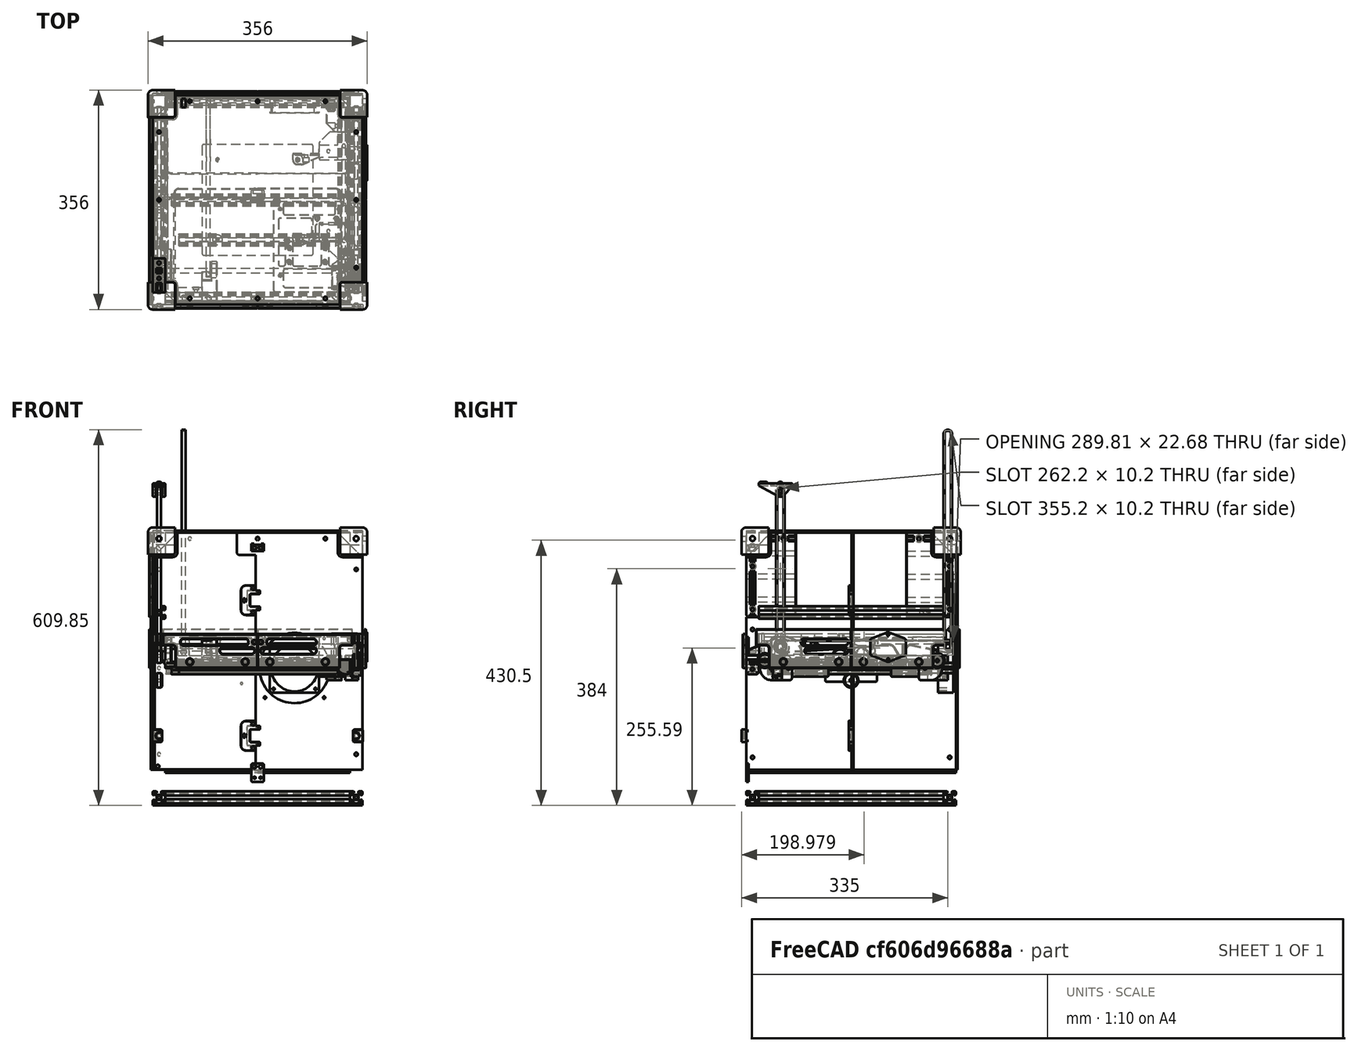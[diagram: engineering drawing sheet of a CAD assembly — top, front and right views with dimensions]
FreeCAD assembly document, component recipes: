
FREECAD ASSEMBLY — COMPONENT RECIPES ("assembly")

This assembly document has 26 components, labeled P0..P25 below (a component is one placed body or linked part). 25 of them carry a construction recipe — the FreeCAD feature program that regenerates the part from scratch, quoted from this document or its linked companion documents; the rest are supplied as boundary geometry only. No exploded tour is included for this assembly.
NOTE — document 3 of 3 of this assembly tour. The two overview renders and the header above are repeated from document 1; the component sections below continue where the previous document stopped.
COMPONENT P24 — recipe-attached ("frame", modeled in this document).
Construction recipe (the document's own serialized feature program — sketch geometry with constraints, then the solid features built on it; lengths are millimeters unless a unit is written):

FEATURE [PartDesign::Mirrored] Mirrored004
  MirrorPlane = -> YZ_Plane006
  Suppressed = false
  TransformMode = 0
FEATURE [PartDesign::Mirrored] Mirrored005
  MirrorPlane = -> XZ_Plane006
  Suppressed = false
  TransformMode = 0
FEATURE [Sketcher::SketchObject] Sketch
  ArcFitTolerance = 0
  AttachmentSupport = -> [XY_Plane005]
  FullyConstrained = true
  MakeInternals = false
  MapMode = 5
  sketch-geometry (22):
    g0: ArcOfCircle CenterX=-9 CenterY=9 CenterZ=0 NormalX=0 NormalY=0 NormalZ=1 AngleXU=0 Radius=1 StartAngle=1.5708 EndAngle=2.35619
    g1: LineSegment StartX=-9 StartY=10 StartZ=0 EndX=-4.90355 EndY=10 EndZ=0
    g2: LineSegment StartX=-4.55 StartY=9.85355 StartZ=0 EndX=-3.12322 EndY=8.42678 EndZ=0
    g3: LineSegment StartX=-3.3 StartY=8 StartZ=0 EndX=-5.75 EndY=8 EndZ=0
    g4: LineSegment StartX=-5.85355 StartY=6.91421 StartZ=0 EndX=-3.08579 EndY=4.14645 EndZ=0
    g5: LineSegment StartX=-2.73223 StartY=4 StartZ=0 EndX=0 EndY=4 EndZ=0
    g6: LineSegment StartX=-6 StartY=7.75 StartZ=0 EndX=-6 EndY=7.26777 EndZ=0
    g7: ArcOfCircle CenterX=-3.3 CenterY=8.25 CenterZ=0 NormalX=0 NormalY=0 NormalZ=1 AngleXU=0 Radius=0.25 StartAngle=4.71239 EndAngle=7.06858
    g8: ArcOfCircle CenterX=-4.90355 CenterY=9.5 CenterZ=0 NormalX=0 NormalY=0 NormalZ=1 AngleXU=0 Radius=0.5 StartAngle=0.785398 EndAngle=1.5708
    g9: GeomPoint [constr] X=-3.05 Y=8.25 Z=0
    g10: ArcOfCircle CenterX=-2.73223 CenterY=4.5 CenterZ=0 NormalX=0 NormalY=0 NormalZ=1 AngleXU=0 Radius=0.5 StartAngle=3.92699 EndAngle=4.71239
    g11: GeomPoint [constr] X=-2.93934 Y=4 Z=0
    g12: ArcOfCircle CenterX=-5.5 CenterY=7.26777 CenterZ=0 NormalX=0 NormalY=0 NormalZ=1 AngleXU=0 Radius=0.5 StartAngle=3.14159 EndAngle=3.92699
    g13: GeomPoint [constr] X=-6 Y=7.06066 Z=0
    g14: ArcOfCircle CenterX=-5.75 CenterY=7.75 CenterZ=0 NormalX=0 NormalY=0 NormalZ=1 AngleXU=0 Radius=0.25 StartAngle=1.5708 EndAngle=3.14159
    g15: GeomPoint [constr] X=-6 Y=8 Z=0
    g16: ArcOfCircle CenterX=0 CenterY=0 CenterZ=0 NormalX=0 NormalY=0 NormalZ=1 AngleXU=0 Radius=2.75 StartAngle=1.5708 EndAngle=2.35619
    g17: GeomPoint [constr] X=0 Y=10 Z=0
    g18: GeomPoint [constr] X=-10 Y=10 Z=0
    g19: LineSegment StartX=-9.70711 StartY=9.70711 StartZ=0 EndX=-1.94454 EndY=1.94454 EndZ=0
    g20: LineSegment StartX=2e-16 StartY=2.75 StartZ=0 EndX=0 EndY=4 EndZ=0
    g21: LineSegment [constr] StartX=-4.46967 StartY=5.53033 StartZ=0 EndX=-5 EndY=5 EndZ=0
  constraints (55):
    c: Radius(g0) = 1
    c: Horizontal(g3)
    c: Parallel(g2,g4)
    c: Vertical(g6)
    c: Tangent(g2,g7) = 1.5708
    c: Tangent(g3,g7) = 1.5708
    c: Tangent(g1,g8) = 1.5708
    c: Tangent(g2,g8) = 1.5708
    c: Radius(g7) = 0.25
    c: Tangent(g1,g0) = 1.5708
    c: PointOnObject(g9,g7)
    c: Horizontal(g9,g7)
    c: PointOnObject(g11,g4)
    c: PointOnObject(g11,g5)
    c: Tangent(g4,g10) = -1.5708
    c: Tangent(g5,g10) = -1.5708
    c: PointOnObject(g13,g4)
    c: PointOnObject(g13,g6)
    c: Tangent(g4,g12) = -1.5708
    c: Tangent(g6,g12) = -1.5708
    c: PointOnObject(g15,g3)
    c: PointOnObject(g15,g6)
    c: Tangent(g3,g14) = -1.5708
    c: Tangent(g6,g14) = -1.5708
    c: Equal(g10,g12)
    c: PointOnObject(g5,g-2)
    c: Coincident(g16,g-1)
    c: PointOnObject(g16,g-2)
    c: PointOnObject(g17,g-2)
    c: PointOnObject(g17,g1)
    c: PointOnObject(g18,g1)
    c: Coincident(g19,g0)
    c: Coincident(g16,g19)
    c: PointOnObject(g0,g19)
    c: PointOnObject(g18,g19)
    c: Parallel(g19,g4)
    c: DistanceX(g18) = -10
    c: DistanceY(g18) = 10
    c: PointOnObject(g16,g19)
    c: Horizontal(g5)
    c: Coincident(g20,g16)
    c: Coincident(g20,g5)
    c: Horizontal(g1)
    c: DistanceX(g15) = -6
    c: DistanceX(g9) = -3.05
    c: DistanceY(g3,g1) = 2
    c: Radius(g10) = 0.5
    c: Radius(g16) = 2.75
    c: DistanceY(g5) = 4
    c: PointOnObject(g21,g4)
    c: Perpendicular(g19,g21)
    c: Distance(g21) = 0.75
    c: Symmetric(g16,g18,g21)
    c: Equal(g14,g7)
    c: Equal(g8,g12)
FEATURE [PartDesign::ShapeBinder] ShapeBinder001
  Support = -> [Sketch]
  TraceSupport = false
FEATURE [PartDesign::Pad] Pad001
  Direction = (0,0,1)
  Length = 440
  Length2 = 10
  Midplane = true
  Profile = -> ShapeBinder001
  Suppressed = false
  Type = 0
  expr: Length = Spreadsheet.height
FEATURE [PartDesign::Mirrored] Mirrored003
  MirrorPlane = -> Pad001 [Face4]
  Suppressed = false
  TransformMode = 0
FEATURE [PartDesign::MultiTransform] MultiTransform001
  BaseFeature = -> Pad001
  Originals = -> [Pad001]
  Refine = true
  Suppressed = false
  TransformMode = 0
  Transformations = -> [Mirrored003,Mirrored004,Mirrored005]
FEATURE [PartDesign::Body] Body001  label="vertical-extrusion"
  AllowCompound = false
  Group = -> [ShapeBinder001,Pad001,MultiTransform001,Mirrored003,Mirrored004,Mirrored005]
  Origin = -> Origin006
  Placement = pos=(160,160,0) rot=(0,0,1;0rad)
  Tip = -> MultiTransform001
  expr: .Placement.Base.x = Spreadsheet.side_length / 2 - 10
  expr: .Placement.Base.y = Spreadsheet.side_length / 2 - 10
FEATURE [PartDesign::Pad] Pad
  Direction = (0,0,1)
  Length = 300
  Length2 = 10
  Midplane = true
  Profile = -> Sketch
  ReferenceAxis = -> Sketch [N_Axis]
  Suppressed = false
  Type = 0
  expr: Length = Spreadsheet.side_length - 40
FEATURE [PartDesign::Mirrored] Mirrored
  MirrorPlane = -> Pad [Face4]
  Suppressed = false
  TransformMode = 0
FEATURE [PartDesign::Mirrored] Mirrored001
  MirrorPlane = -> Sketch [V_Axis]
  Suppressed = false
  TransformMode = 0
FEATURE [PartDesign::Mirrored] Mirrored002
  MirrorPlane = -> XZ_Plane005
  Suppressed = false
  TransformMode = 0
FEATURE [PartDesign::MultiTransform] MultiTransform
  BaseFeature = -> Pad
  Originals = -> [Pad]
  Refine = true
  Suppressed = false
  TransformMode = 0
  Transformations = -> [Mirrored,Mirrored001,Mirrored002]
FEATURE [PartDesign::Body] Body  label="horizontal-extrusion"
  AllowCompound = false
  Group = -> [Sketch,Pad,MultiTransform,Mirrored,Mirrored001,Mirrored002]
  Origin = -> Origin005
  Placement = pos=(0,160,210) rot=(0,1,0;1.5708rad)
  Tip = -> MultiTransform
  expr: .Placement.Base.y = Spreadsheet.side_length / 2 - 10
  expr: .Placement.Base.z = Spreadsheet.height / 2 - 10
FEATURE [Sketcher::SketchObject] Sketch405
  ArcFitTolerance = 1e-06
  AttachmentSupport = -> [XY_Plane267]
  FullyConstrained = true
  MakeInternals = false
  MapMode = 5
  expr: Constraints[18] = Spreadsheet.side_length
  expr: Constraints[9] = Spreadsheet.side_length - 40
  sketch-geometry (8):
    g0: LineSegment [constr] StartX=-150 StartY=170 StartZ=0 EndX=-150 EndY=-170 EndZ=0
    g1: LineSegment [constr] StartX=-150 StartY=-170 StartZ=0 EndX=150 EndY=-170 EndZ=0
    g2: LineSegment [constr] StartX=150 StartY=-170 StartZ=0 EndX=150 EndY=170 EndZ=0
    g3: LineSegment [constr] StartX=150 StartY=170 StartZ=0 EndX=-150 EndY=170 EndZ=0
    g4: LineSegment StartX=-150 StartY=170 StartZ=0 EndX=150 EndY=170 EndZ=0
    g5: LineSegment StartX=150 StartY=170 StartZ=0 EndX=150 EndY=-170 EndZ=0
    g6: LineSegment StartX=150 StartY=-170 StartZ=0 EndX=-150 EndY=-170 EndZ=0
    g7: LineSegment StartX=-150 StartY=-170 StartZ=0 EndX=-150 EndY=170 EndZ=0
  constraints (19):
    c: Coincident(g0,g1)
    c: Coincident(g1,g2)
    c: Coincident(g2,g3)
    c: Coincident(g3,g0)
    c: Vertical(g0)
    c: Vertical(g2)
    c: Horizontal(g1)
    c: Horizontal(g3)
    c: Symmetric(g1,g0,g-1)
    c: DistanceX(g3,g3) = 300
    c: Coincident(g7,g0)
    c: Coincident(g7,g4)
    c: Coincident(g5,g2)
    c: Coincident(g5,g4)
    c: Coincident(g7,g0)
    c: Coincident(g7,g6)
    c: Coincident(g6,g1)
    c: Coincident(g6,g5)
    c: DistanceY(g5,g5) = 340
FEATURE [PartDesign::Pad] Pad088
  Direction = (0,0,1)
  Length = 3
  Length2 = 10
  Profile = -> Sketch405
  ReferenceAxis = -> Sketch405 [N_Axis]
  Suppressed = false
  Type = 0
FEATURE [Sketcher::SketchObject] Sketch406
  ArcFitTolerance = 1e-06
  AttachmentSupport = -> [XY_Plane267]
  FullyConstrained = true
  MakeInternals = false
  MapMode = 5
  expr: Constraints[0] = Spreadsheet.side_length / 2
  sketch-geometry (7):
    g0: GeomPoint X=170 Y=170 Z=0
    g1: LineSegment [constr] StartX=170 StartY=0 StartZ=0 EndX=170 EndY=170 EndZ=0
    g2: LineSegment [constr] StartX=170 StartY=170 StartZ=0 EndX=0 EndY=170 EndZ=0
    g3: LineSegment StartX=170 StartY=170 StartZ=0 EndX=150 EndY=170 EndZ=0
    g4: LineSegment StartX=150 StartY=170 StartZ=0 EndX=150 EndY=150 EndZ=0
    g5: LineSegment StartX=150 StartY=150 StartZ=0 EndX=170 EndY=150 EndZ=0
    g6: LineSegment StartX=170 StartY=150 StartZ=0 EndX=170 EndY=170 EndZ=0
  constraints (19):
    c: DistanceX(g0) = 170
    c: PointOnObject(g1,g-1)
    c: Coincident(g1,g0)
    c: Vertical(g1)
    c: Coincident(g1,g2)
    c: PointOnObject(g2,g-2)
    c: Horizontal(g2)
    c: Equal(g2,g1)
    c: Coincident(g3,g0)
    c: PointOnObject(g3,g2)
    c: Coincident(g3,g4)
    c: Vertical(g4)
    c: PointOnObject(g5,g1)
    c: Horizontal(g5)
    c: Coincident(g5,g6)
    c: Coincident(g6,g3)
    c: Equal(g5,g4)
    c: DistanceY(g4,g4) = 20
    c: Coincident(g5,g4)
FEATURE [PartDesign::Pocket] Pocket281
  BaseFeature = -> Pad088
  Direction = (0,0,-1)
  Length = 5
  Length2 = 5
  Midplane = true
  Profile = -> Sketch406
  ReferenceAxis = -> Sketch406 [N_Axis]
  Suppressed = false
  Type = 1
FEATURE [PartDesign::PolarPattern] PolarPattern004
  Angle = 360
  Axis = -> Z_Axis267
  BaseFeature = -> Pocket281
  Mode = 0
  Occurrences = 4
  Offset = 120
  Originals = -> [Pocket281]
  Suppressed = false
  TransformMode = 0
FEATURE [Sketcher::SketchObject] Sketch407
  ArcFitTolerance = 1e-06
  AttachmentSupport = -> [XY_Plane267]
  FullyConstrained = true
  MakeInternals = false
  MapMode = 5
  expr: Constraints[22] = Spreadsheet.side_length / 2
  sketch-geometry (14):
    g0: LineSegment StartX=115 StartY=170 StartZ=0 EndX=115 EndY=149 EndZ=0
    g1: LineSegment StartX=115 StartY=149 StartZ=0 EndX=125 EndY=149 EndZ=0
    g2: LineSegment StartX=125 StartY=149 StartZ=0 EndX=125 EndY=170 EndZ=0
    g3: LineSegment StartX=125 StartY=170 StartZ=0 EndX=115 EndY=170 EndZ=0
    g4: LineSegment StartX=154 StartY=-105 StartZ=0 EndX=154 EndY=-125 EndZ=0
    g5: LineSegment StartX=154 StartY=-125 StartZ=0 EndX=170 EndY=-125 EndZ=0
    g6: LineSegment StartX=170 StartY=-125 StartZ=0 EndX=170 EndY=-105 EndZ=0
    g7: LineSegment StartX=170 StartY=-105 StartZ=0 EndX=154 EndY=-105 EndZ=0
    g8: GeomPoint X=170 Y=-170 Z=0
    g9: GeomPoint X=170 Y=170 Z=0
    g10: LineSegment [constr] StartX=0 StartY=-170 StartZ=0 EndX=170 EndY=-170 EndZ=0
    g11: LineSegment [constr] StartX=170 StartY=-170 StartZ=0 EndX=170 EndY=0 EndZ=0
    g12: GeomPoint [constr] X=120 Y=170 Z=0
    g13: GeomPoint [constr] X=170 Y=-115 Z=0
  constraints (35):
    c: Coincident(g0,g1)
    c: Coincident(g1,g2)
    c: Coincident(g2,g3)
    c: Coincident(g3,g0)
    c: Vertical(g0)
    c: Vertical(g2)
    c: Horizontal(g1)
    c: Horizontal(g3)
    c: Coincident(g4,g5)
    c: Coincident(g5,g6)
    c: Coincident(g6,g7)
    c: Coincident(g7,g4)
    c: Vertical(g4)
    c: Vertical(g6)
    c: Horizontal(g5)
    c: Horizontal(g7)
    c: PointOnObject(g10,g-2)
    c: Coincident(g10,g8)
    c: Coincident(g10,g11)
    c: PointOnObject(g11,g-1)
    c: Vertical(g11)
    c: Horizontal(g10)
    c: DistanceX(g8) = 170
    c: Equal(g11,g10)
    c: Symmetric(g9,g8,g-1)
    c: PointOnObject(g5,g11)
    c: DistanceX(g5,g5) = 16
    c: DistanceX(g3,g3) = 10
    c: Horizontal(g2,g9)
    c: Symmetric(g3,g3,g12)
    c: DistanceX(g12,g9) = 50
    c: DistanceY(g2,g2) = 21
    c: Symmetric(g6,g6,g13)
    c: DistanceY(g8,g13) = 55
    c: DistanceY(g4,g4) = 20
FEATURE [PartDesign::Pocket] Pocket282
  BaseFeature = -> PolarPattern004
  Direction = (0,0,-1)
  Length = 5
  Length2 = 5
  Midplane = true
  Profile = -> Sketch407
  ReferenceAxis = -> Sketch407 [N_Axis]
  Suppressed = false
  Type = 1
FEATURE [PartDesign::Mirrored] Mirrored009
  BaseFeature = -> Pocket282
  MirrorPlane = -> YZ_Plane267
  Originals = -> [Pocket282]
  Suppressed = false
  TransformMode = 0
FEATURE [Sketcher::SketchObject] Sketch426
  ArcFitTolerance = 1e-06
  AttachmentSupport = -> [XZ_Plane280]
  FullyConstrained = true
  MakeInternals = false
  MapMode = 5
  Placement = pos=(0,0,0) rot=(1,0,0;1.5708rad)
  expr: Constraints[10] = Spreadsheet.height
  expr: Constraints[7] = Spreadsheet.side_length
  sketch-geometry (5):
    g0: LineSegment StartX=-170 StartY=220 StartZ=0 EndX=-170 EndY=-165 EndZ=0
    g1: LineSegment StartX=-170 StartY=-165 StartZ=0 EndX=170 EndY=-165 EndZ=0
    g2: LineSegment StartX=170 StartY=-165 StartZ=0 EndX=170 EndY=220 EndZ=0
    g3: LineSegment StartX=170 StartY=220 StartZ=0 EndX=-170 EndY=220 EndZ=0
    g4: GeomPoint X=170 Y=-220 Z=0
  constraints (12):
    c: Coincident(g0,g1)
    c: Coincident(g1,g2)
    c: Coincident(g2,g3)
    c: Coincident(g3,g0)
    c: Vertical(g0)
    c: Vertical(g2)
    c: Horizontal(g1)
    c: DistanceX(g3,g3) = 340
    c: Symmetric(g2,g0,g-2)
    c: Symmetric(g4,g2,g-1)
    c: DistanceY(g4,g2) = 440
    c: DistanceY(g4,g1) = 55
FEATURE [PartDesign::Pad] Pad091
  Direction = (0,-1,2e-16)
  Length = 3
  Length2 = 10
  Placement = pos=(0,0,0) rot=(1,0,0;1.5708rad)
  Profile = -> Sketch426
  ReferenceAxis = -> Sketch426 [N_Axis]
  Reversed = true
  Suppressed = false
  Type = 0
FEATURE [Sketcher::SketchObject] Sketch427
  ArcFitTolerance = 1e-06
  AttachmentSupport = -> [XZ_Plane280]
  FullyConstrained = true
  MakeInternals = false
  MapMode = 5
  Placement = pos=(0,0,0) rot=(1,0,0;1.5708rad)
  expr: Constraints[0] = Spreadsheet.height / 2
  expr: Constraints[1] = Spreadsheet.side_length / 2
  sketch-geometry (11):
    g0: GeomPoint X=170 Y=220 Z=0
    g1: LineSegment StartX=133.5 StartY=187.5 StartZ=0 EndX=133.5 EndY=220 EndZ=0
    g2: LineSegment StartX=133.5 StartY=220 StartZ=0 EndX=170 EndY=220 EndZ=0
    g3: LineSegment StartX=170 StartY=220 StartZ=0 EndX=170 EndY=183.5 EndZ=0
    g4: LineSegment StartX=170 StartY=183.5 StartZ=0 EndX=137.5 EndY=183.5 EndZ=0
    g5: ArcOfCircle CenterX=137.5 CenterY=187.5 CenterZ=0 NormalX=0 NormalY=0 NormalZ=1 AngleXU=0 Radius=4 StartAngle=3.14159 EndAngle=4.71239
    g6: Circle CenterX=0 CenterY=210 CenterZ=0 NormalX=0 NormalY=0 NormalZ=1 AngleXU=0 Radius=2.75
    g7: Circle CenterX=110 CenterY=210 CenterZ=0 NormalX=0 NormalY=0 NormalZ=1 AngleXU=0 Radius=2.75
    g8: Circle CenterX=160 CenterY=160 CenterZ=0 NormalX=0 NormalY=0 NormalZ=1 AngleXU=0 Radius=2.75
    g9: Circle CenterX=160 CenterY=0 CenterZ=0 NormalX=0 NormalY=0 NormalZ=1 AngleXU=0 Radius=2.75
    g10: Circle CenterX=160 CenterY=-140 CenterZ=0 NormalX=0 NormalY=0 NormalZ=1 AngleXU=0 Radius=2.75
  constraints (30):
    c: DistanceY(g0) = 220
    c: DistanceX(g0) = 170
    c: Vertical(g1)
    c: Coincident(g1,g2)
    c: Coincident(g2,g0)
    c: Horizontal(g2)
    c: Coincident(g2,g3)
    c: Vertical(g3)
    c: Coincident(g3,g4)
    c: Tangent(g5,g1) = 1.5708
    c: Tangent(g5,g4) = 1.5708
    c: Horizontal(g4)
    c: DistanceY(g3,g3) = 36.5
    c: Equal(g2,g3)
    c: Radius(g5) = 4
    c: PointOnObject(g6,g-2)
    c: PointOnObject(g9,g-1)
    c: Equal(g7,g8)
    c: Equal(g8,g9)
    c: Equal(g9,g6)
    c: Diameter(g6) = 5.5
    c: Horizontal(g6,g7)
    c: DistanceY(g7,g0) = 10
    c: DistanceX(g7,g0) = 60
    c: DistanceX(g8,g0) = 10
    c: DistanceY(g8,g0) = 60
    c: DistanceY(g10) = -140
    c: Vertical(g10,g9)
    c: Equal(g9,g10)
    c: Vertical(g9,g8)
FEATURE [PartDesign::Pocket] Pocket299
  BaseFeature = -> Pad091
  Direction = (0,1,-2e-16)
  Length = 5
  Length2 = 5
  Placement = pos=(0,0,0) rot=(1,0,0;1.5708rad)
  Profile = -> Sketch427
  ReferenceAxis = -> Sketch427 [N_Axis]
  Suppressed = false
  Type = 1
FEATURE [PartDesign::Mirrored] Mirrored010
  BaseFeature = -> Pocket299
  MirrorPlane = -> YZ_Plane280
  Originals = -> [Pocket299]
  Placement = pos=(0,0,0) rot=(1,0,0;1.5708rad)
  Suppressed = false
  TransformMode = 0
FEATURE [Sketcher::SketchObject] Sketch428
  ArcFitTolerance = 1e-06
  AttachmentSupport = -> [YZ_Plane281]
  FullyConstrained = true
  MakeInternals = false
  MapMode = 5
  Placement = pos=(0,0,0) rot=(0.57735,0.57735,0.57735;2.0944rad)
  expr: Constraints[10] = Spreadsheet.height
  expr: Constraints[28] = Spreadsheet.xy_gantry_height
  expr: Constraints[9] = Spreadsheet.side_length
  sketch-geometry (33):
    g0: GeomPoint X=170 Y=-220 Z=0
    g1: LineSegment [constr] StartX=-170 StartY=220 StartZ=0 EndX=-170 EndY=-165 EndZ=0
    g2: LineSegment StartX=-170 StartY=-165 StartZ=0 EndX=170 EndY=-165 EndZ=0
    g3: LineSegment [constr] StartX=170 StartY=-165 StartZ=0 EndX=170 EndY=220 EndZ=0
    g4: LineSegment [constr] StartX=170 StartY=220 StartZ=0 EndX=-170 EndY=220 EndZ=0
    g5: LineSegment StartX=-170 StartY=-165 StartZ=0 EndX=-170 EndY=82.5 EndZ=0
    g6: LineSegment StartX=-170 StartY=82.5 StartZ=0 EndX=-93.7 EndY=82.5 EndZ=0
    g7: LineSegment StartX=-89.7 StartY=86.5 StartZ=0 EndX=-89.7 EndY=220 EndZ=0
    g8: LineSegment StartX=-89.7 StartY=220 StartZ=0 EndX=89.7 EndY=220 EndZ=0
    g9: LineSegment StartX=89.7 StartY=220 StartZ=0 EndX=89.7 EndY=86.5 EndZ=0
    g10: LineSegment StartX=93.7 StartY=82.5 StartZ=0 EndX=170 EndY=82.5 EndZ=0
    g11: LineSegment StartX=170 StartY=82.5 StartZ=0 EndX=170 EndY=-165 EndZ=0
    g12: GeomPoint X=170 Y=90 Z=0
    g13: ArcOfCircle CenterX=-93.7 CenterY=86.5 CenterZ=0 NormalX=0 NormalY=0 NormalZ=1 AngleXU=0 Radius=4 StartAngle=4.71239 EndAngle=6.28319
    g14: GeomPoint [constr] X=-89.7 Y=82.5 Z=0
    g15: ArcOfCircle CenterX=93.7 CenterY=86.5 CenterZ=0 NormalX=0 NormalY=0 NormalZ=1 AngleXU=0 Radius=4 StartAngle=3.14159 EndAngle=4.71239
    g16: GeomPoint [constr] X=89.7 Y=82.5 Z=0
    g17: Circle CenterX=-160 CenterY=62.5 CenterZ=0 NormalX=0 NormalY=0 NormalZ=1 AngleXU=0 Radius=2.75
    g18: Circle CenterX=-160 CenterY=-145 CenterZ=0 NormalX=0 NormalY=0 NormalZ=1 AngleXU=0 Radius=2.75
    g19: Circle CenterX=160 CenterY=-145 CenterZ=0 NormalX=0 NormalY=0 NormalZ=1 AngleXU=0 Radius=2.75
    g20: Circle CenterX=160 CenterY=62.5 CenterZ=0 NormalX=0 NormalY=0 NormalZ=1 AngleXU=0 Radius=2.75
    g21: LineSegment StartX=-42.1 StartY=20.1 StartZ=0 EndX=-42.1 EndY=-20.1 EndZ=0
    g22: LineSegment StartX=-40.1 StartY=-22.1 StartZ=0 EndX=40.1 EndY=-22.1 EndZ=0
    g23: LineSegment StartX=42.1 StartY=-20.1 StartZ=0 EndX=42.1 EndY=20.1 EndZ=0
    g24: LineSegment StartX=40.1 StartY=22.1 StartZ=0 EndX=-40.1 EndY=22.1 EndZ=0
    g25: ArcOfCircle CenterX=40.1 CenterY=20.1 CenterZ=0 NormalX=0 NormalY=0 NormalZ=1 AngleXU=0 Radius=2 StartAngle=5e-16 EndAngle=1.5708
    g26: GeomPoint [constr] X=42.1 Y=22.1 Z=0
    g27: ArcOfCircle CenterX=40.1 CenterY=-20.1 CenterZ=0 NormalX=0 NormalY=0 NormalZ=1 AngleXU=0 Radius=2 StartAngle=4.71239 EndAngle=6.28319
    g28: GeomPoint [constr] X=42.1 Y=-22.1 Z=0
    g29: ArcOfCircle CenterX=-40.1 CenterY=-20.1 CenterZ=0 NormalX=0 NormalY=0 NormalZ=1 AngleXU=0 Radius=2 StartAngle=3.14159 EndAngle=4.71239
    g30: GeomPoint [constr] X=-42.1 Y=-22.1 Z=0
    g31: ArcOfCircle CenterX=-40.1 CenterY=20.1 CenterZ=0 NormalX=0 NormalY=0 NormalZ=1 AngleXU=0 Radius=2 StartAngle=1.5708 EndAngle=3.14159
    g32: GeomPoint [constr] X=-42.1 Y=22.1 Z=0
  constraints (78):
    c: Coincident(g1,g2)
    c: Coincident(g2,g3)
    c: Coincident(g3,g4)
    c: Coincident(g4,g1)
    c: Vertical(g1)
    c: Vertical(g3)
    c: Horizontal(g2)
    c: Symmetric(g3,g0,g-1)
    c: Symmetric(g3,g1,g-2)
    c: DistanceX(g4,g4) = 340
    c: DistanceY(g0,g3) = 440
    c: DistanceY(g0,g2) = 55
    c: Coincident(g1,g5)
    c: PointOnObject(g5,g1)
    c: Coincident(g5,g6)
    c: Horizontal(g6)
    c: PointOnObject(g7,g4)
    c: Vertical(g7)
    c: Coincident(g7,g8)
    c: PointOnObject(g8,g4)
    c: Coincident(g8,g9)
    c: Vertical(g9)
    c: PointOnObject(g10,g3)
    c: Horizontal(g10)
    c: Coincident(g10,g11)
    c: Coincident(g11,g2)
    c: Symmetric(g16,g14,g-2)
    c: PointOnObject(g12,g3)
    c: DistanceY(g0,g12) = 310
    c: DistanceY(g10,g12) = 7.5
    c: DistanceX(g16,g10) = 80.3
    c: PointOnObject(g14,g6)
    c: PointOnObject(g14,g7)
    c: Tangent(g6,g13) = -1.5708
    c: Tangent(g7,g13) = -1.5708
    c: PointOnObject(g16,g9)
    c: PointOnObject(g16,g10)
    c: Tangent(g9,g15) = -1.5708
    c: Tangent(g10,g15) = -1.5708
    c: Equal(g15,g13)
    c: Radius(g13) = 4
    c: Symmetric(g20,g17,g-2)
    c: Symmetric(g19,g18,g-2)
    c: Equal(g18,g19)
    c: Equal(g19,g20)
    c: Equal(g20,g17)
    c: Diameter(g17) = 5.5
    c: DistanceY(g17,g5) = 20
    c: DistanceX(g5,g17) = 10
    c: DistanceY(g1,g18) = 20
    c: Vertical(g18,g17)
    c: Vertical(g21)
    c: Vertical(g23)
    c: Horizontal(g22)
    c: Horizontal(g24)
    c: Symmetric(g32,g28,g-1)
    c: DistanceY(g28,g26) = 44.2
    c: DistanceX(g32,g26) = 84.2
    c: PointOnObject(g26,g23)
    c: PointOnObject(g26,g24)
    c: Tangent(g23,g25) = -1.5708
    c: Tangent(g24,g25) = -1.5708
    c: PointOnObject(g28,g22)
    c: PointOnObject(g28,g23)
    c: Tangent(g22,g27) = -1.5708
    c: Tangent(g23,g27) = -1.5708
    c: PointOnObject(g30,g21)
    c: PointOnObject(g30,g22)
    c: Tangent(g21,g29) = -1.5708
    c: Tangent(g22,g29) = -1.5708
    c: PointOnObject(g32,g21)
    c: PointOnObject(g32,g24)
    c: Tangent(g21,g31) = -1.5708
    c: Tangent(g24,g31) = -1.5708
    c: Equal(g25,g31)
    c: Equal(g31,g29)
    c: Equal(g29,g27)
    c: Radius(g27) = 2
FEATURE [PartDesign::Pad] Pad092
  Direction = (1,0,0)
  Length = 3
  Length2 = 10
  Placement = pos=(0,0,0) rot=(1,1,1;2.0944rad)
  Profile = -> Sketch428
  ReferenceAxis = -> Sketch428 [N_Axis]
  Suppressed = false
  Type = 0
FEATURE [PartDesign::Body] Body144  label="panel-right"
  AllowCompound = false
  Group = -> [Sketch428,Pad092]
  Origin = -> Origin282
  Placement = pos=(170,0,0) rot=(0,0,1;0rad)
  Tip = -> Pad092
  expr: .Placement.Base.x = Spreadsheet.side_length / 2
FEATURE [Sketcher::SketchObject] Sketch429
  ArcFitTolerance = 1e-06
  AttachmentSupport = -> [XY_Plane282]
  FullyConstrained = true
  MakeInternals = false
  MapMode = 5
  expr: Constraints[10] = Spreadsheet.side_length
  sketch-geometry (4):
    g0: LineSegment StartX=-170 StartY=170 StartZ=0 EndX=-170 EndY=-170 EndZ=0
    g1: LineSegment StartX=-170 StartY=-170 StartZ=0 EndX=170 EndY=-170 EndZ=0
    g2: LineSegment StartX=170 StartY=-170 StartZ=0 EndX=170 EndY=170 EndZ=0
    g3: LineSegment StartX=170 StartY=170 StartZ=0 EndX=-170 EndY=170 EndZ=0
  constraints (11):
    c: Coincident(g0,g1)
    c: Coincident(g1,g2)
    c: Coincident(g2,g3)
    c: Coincident(g3,g0)
    c: Vertical(g0)
    c: Vertical(g2)
    c: Horizontal(g1)
    c: Horizontal(g3)
    c: Symmetric(g1,g0,g-1)
    c: Equal(g2,g3)
    c: DistanceX(g3,g3) = 340
FEATURE [PartDesign::Pad] Pad093
  Direction = (0,0,1)
  Length = 3
  Length2 = 10
  Profile = -> Sketch429
  ReferenceAxis = -> Sketch429 [N_Axis]
  Suppressed = false
  Type = 0
FEATURE [Sketcher::SketchObject] Sketch430
  ArcFitTolerance = 1e-06
  AttachmentSupport = -> [XY_Plane282]
  FullyConstrained = true
  MakeInternals = false
  MapMode = 5
  expr: Constraints[0] = Spreadsheet.side_length / 2
  sketch-geometry (12):
    g0: GeomPoint X=170 Y=170 Z=0
    g1: LineSegment [constr] StartX=170 StartY=0 StartZ=0 EndX=170 EndY=170 EndZ=0
    g2: LineSegment [constr] StartX=170 StartY=170 StartZ=0 EndX=0 EndY=170 EndZ=0
    g3: LineSegment StartX=170 StartY=170 StartZ=0 EndX=133.5 EndY=170 EndZ=0
    g4: LineSegment StartX=133.5 StartY=170 StartZ=0 EndX=133.5 EndY=137.5 EndZ=0
    g5: LineSegment StartX=137.5 StartY=133.5 StartZ=0 EndX=170 EndY=133.5 EndZ=0
    g6: LineSegment StartX=170 StartY=133.5 StartZ=0 EndX=170 EndY=170 EndZ=0
    g7: ArcOfCircle CenterX=137.5 CenterY=137.5 CenterZ=0 NormalX=0 NormalY=0 NormalZ=1 AngleXU=0 Radius=4 StartAngle=3.14159 EndAngle=4.71239
    g8: GeomPoint [constr] X=133.5 Y=133.5 Z=0
    g9: Circle CenterX=110 CenterY=160 CenterZ=0 NormalX=0 NormalY=0 NormalZ=1 AngleXU=0 Radius=2.75
    g10: Circle CenterX=160 CenterY=110 CenterZ=0 NormalX=0 NormalY=0 NormalZ=1 AngleXU=0 Radius=2.75
    g11: Circle CenterX=0 CenterY=160 CenterZ=0 NormalX=0 NormalY=0 NormalZ=1 AngleXU=0 Radius=2.75
  constraints (32):
    c: DistanceX(g0) = 170
    c: PointOnObject(g1,g-1)
    c: Coincident(g1,g0)
    c: Coincident(g1,g2)
    c: PointOnObject(g2,g-2)
    c: Horizontal(g2)
    c: Vertical(g1)
    c: Equal(g2,g1)
    c: Coincident(g3,g4)
    c: Coincident(g5,g6)
    c: Coincident(g6,g3)
    c: Horizontal(g3)
    c: Horizontal(g5)
    c: Vertical(g4)
    c: Vertical(g6)
    c: Coincident(g3,g0)
    c: Equal(g6,g3)
    c: DistanceX(g3,g3) = 36.5
    c: PointOnObject(g8,g4)
    c: PointOnObject(g8,g5)
    c: Tangent(g4,g7) = -1.5708
    c: Tangent(g5,g7) = -1.5708
    c: Radius(g7) = 4
    c: PointOnObject(g11,g-2)
    c: Equal(g11,g9)
    c: Equal(g9,g10)
    c: Horizontal(g9,g11)
    c: DistanceX(g10,g0) = 10
    c: DistanceY(g9,g0) = 10
    c: Diameter(g9) = 5.5
    c: DistanceY(g10,g0) = 60
    c: DistanceX(g9,g0) = 60
FEATURE [PartDesign::Pocket] Pocket300
  BaseFeature = -> Pad093
  Direction = (0,0,-1)
  Length = 5
  Length2 = 5
  Midplane = true
  Profile = -> Sketch430
  ReferenceAxis = -> Sketch430 [N_Axis]
  Suppressed = false
  Type = 1
FEATURE [PartDesign::PolarPattern] PolarPattern005
  Angle = 360
  Axis = -> Z_Axis282
  BaseFeature = -> Pocket300
  Mode = 0
  Occurrences = 4
  Offset = 120
  Originals = -> [Pocket300]
  Suppressed = false
  TransformMode = 0
FEATURE [PartDesign::Body] Body145  label="panel-top"
  AllowCompound = false
  Group = -> [Sketch429,Pad093,Sketch430,Pocket300,PolarPattern005]
  Origin = -> Origin283
  Placement = pos=(0,0,220) rot=(0,0,1;0rad)
  Tip = -> PolarPattern005
  expr: .Placement.Base.z = Spreadsheet.height / 2
FEATURE [PartDesign::FeatureBase] Clone009
  BaseFeature = -> Body146
  Suppressed = false
FEATURE [PartDesign::Body] Body148
  AllowCompound = false
  Group = -> [Clone009]
  Origin = -> Origin286
  Placement = pos=(-160,-170,110) rot=(0,0,1;0rad)
  Tip = -> Clone009
  expr: .Placement.Base.x = -Spreadsheet.side_length / 2 + 10
  expr: .Placement.Base.y = -Spreadsheet.side_length / 2
FEATURE [Sketcher::SketchObject] Sketch450
  ArcFitTolerance = 1e-06
  AttachmentSupport = -> [XZ_Plane289]
  FullyConstrained = true
  MakeInternals = false
  MapMode = 5
  Placement = pos=(0,0,0) rot=(1,0,0;1.5708rad)
  sketch-geometry (12):
    g0: LineSegment StartX=-10 StartY=8 StartZ=0 EndX=-10 EndY=-18 EndZ=0
    g1: LineSegment StartX=-8 StartY=-20 StartZ=0 EndX=8 EndY=-20 EndZ=0
    g2: LineSegment StartX=10 StartY=-18 StartZ=0 EndX=10 EndY=8 EndZ=0
    g3: LineSegment StartX=8 StartY=10 StartZ=0 EndX=-8 EndY=10 EndZ=0
    g4: ArcOfCircle CenterX=-8 CenterY=8 CenterZ=0 NormalX=0 NormalY=0 NormalZ=1 AngleXU=0 Radius=2 StartAngle=1.5708 EndAngle=3.14159
    g5: GeomPoint [constr] X=-10 Y=10 Z=0
    g6: ArcOfCircle CenterX=8 CenterY=8 CenterZ=0 NormalX=0 NormalY=0 NormalZ=1 AngleXU=0 Radius=2 StartAngle=1e-16 EndAngle=1.5708
    g7: GeomPoint [constr] X=10 Y=10 Z=0
    g8: ArcOfCircle CenterX=8 CenterY=-18 CenterZ=0 NormalX=0 NormalY=0 NormalZ=1 AngleXU=0 Radius=2 StartAngle=4.71239 EndAngle=6.28319
    g9: GeomPoint [constr] X=10 Y=-20 Z=0
    g10: ArcOfCircle CenterX=-8 CenterY=-18 CenterZ=0 NormalX=0 NormalY=0 NormalZ=1 AngleXU=0 Radius=2 StartAngle=3.14159 EndAngle=4.71239
    g11: GeomPoint [constr] X=-10 Y=-20 Z=0
  constraints (27):
    c: Vertical(g0)
    c: Vertical(g2)
    c: Horizontal(g1)
    c: DistanceY(g7) = 10
    c: Symmetric(g7,g5,g-2)
    c: DistanceX(g5,g7) = 20
    c: DistanceY(g9) = -20
    c: PointOnObject(g5,g0)
    c: PointOnObject(g5,g3)
    c: Tangent(g0,g4) = -1.5708
    c: Tangent(g3,g4) = -1.5708
    c: PointOnObject(g7,g2)
    c: PointOnObject(g7,g3)
    c: Tangent(g2,g6) = -1.5708
    c: Tangent(g3,g6) = -1.5708
    c: PointOnObject(g9,g1)
    c: PointOnObject(g9,g2)
    c: Tangent(g1,g8) = -1.5708
    c: Tangent(g2,g8) = -1.5708
    c: PointOnObject(g11,g0)
    c: PointOnObject(g11,g1)
    c: Tangent(g0,g10) = -1.5708
    c: Tangent(g1,g10) = -1.5708
    c: Equal(g10,g8)
    c: Equal(g10,g6)
    c: Equal(g10,g4)
    c: Radius(g10) = 2
FEATURE [PartDesign::Pad] Pad099
  Direction = (0,-1,2e-16)
  Length = 4
  Length2 = 10
  Placement = pos=(0,0,0) rot=(1,0,0;1.5708rad)
  Profile = -> Sketch450
  ReferenceAxis = -> Sketch450 [N_Axis]
  Reversed = true
  Suppressed = false
  Type = 0
FEATURE [Sketcher::SketchObject] Sketch451
  ArcFitTolerance = 1e-06
  AttachmentOffset = pos=(0,0,-1) rot=(0,0,1;0rad)
  AttachmentSupport = -> [XZ_Plane289]
  FullyConstrained = true
  MakeInternals = false
  MapMode = 5
  Placement = pos=(0,1,-2e-16) rot=(1,0,0;1.5708rad)
  sketch-geometry (14):
    g0: LineSegment StartX=-2.25 StartY=-14.5877 StartZ=0 EndX=-2.25 EndY=-11.4123 EndZ=0
    g1: LineSegment StartX=-2.25 StartY=-11.4123 StartZ=0 EndX=-5 EndY=-9.82457 EndZ=0
    g2: LineSegment StartX=-5 StartY=-9.82457 StartZ=0 EndX=-7.75 EndY=-11.4123 EndZ=0
    g3: LineSegment StartX=-7.75 StartY=-11.4123 StartZ=0 EndX=-7.75 EndY=-14.5877 EndZ=0
    g4: LineSegment StartX=-7.75 StartY=-14.5877 StartZ=0 EndX=-5 EndY=-16.1754 EndZ=0
    g5: LineSegment StartX=-5 StartY=-16.1754 StartZ=0 EndX=-2.25 EndY=-14.5877 EndZ=0
    g6: Circle [constr] CenterX=-5 CenterY=-13 CenterZ=0 NormalX=0 NormalY=0 NormalZ=1 AngleXU=0 Radius=3.17543
    g7: LineSegment StartX=7.75 StartY=-14.5877 StartZ=0 EndX=7.75 EndY=-11.4123 EndZ=0
    g8: LineSegment StartX=7.75 StartY=-11.4123 StartZ=0 EndX=5 EndY=-9.82457 EndZ=0
    g9: LineSegment StartX=5 StartY=-9.82457 StartZ=0 EndX=2.25 EndY=-11.4123 EndZ=0
    g10: LineSegment StartX=2.25 StartY=-11.4123 StartZ=0 EndX=2.25 EndY=-14.5877 EndZ=0
    g11: LineSegment StartX=2.25 StartY=-14.5877 StartZ=0 EndX=5 EndY=-16.1754 EndZ=0
    g12: LineSegment StartX=5 StartY=-16.1754 StartZ=0 EndX=7.75 EndY=-14.5877 EndZ=0
    g13: Circle [constr] CenterX=5 CenterY=-13 CenterZ=0 NormalX=0 NormalY=0 NormalZ=1 AngleXU=0 Radius=3.17543
  constraints (33):
    c: Coincident(g0,g1)
    c: Coincident(g1,g2)
    c: Coincident(g2,g3)
    c: Coincident(g3,g4)
    c: Coincident(g4,g5)
    c: Coincident(g5,g0)
    c: Equal(g0, g1-g5) x5
    c: PointOnObject(g0,g6)
    c: PointOnObject(g1,g6)
    c: PointOnObject(g2,g6)
    c: PointOnObject(g3,g6)
    c: PointOnObject(g4,g6)
    c: PointOnObject(g5,g6)
    c: Coincident(g7,g8)
    c: Coincident(g8,g9)
    c: Coincident(g9,g10)
    c: Coincident(g10,g11)
    c: Coincident(g11,g12)
    c: Coincident(g12,g7)
    c: Equal(g7, g8-g12) x5
    c: PointOnObject(g7,g13)
    c: PointOnObject(g8,g13)
    c: PointOnObject(g9,g13)
    c: PointOnObject(g10,g13)
    c: PointOnObject(g11,g13)
    c: PointOnObject(g12,g13)
    c: Vertical(g7)
    c: Vertical(g0)
    c: Symmetric(g13,g6,g-2)
    c: Equal(g13,g6)
    c: DistanceX(g6,g13) = 10
    c: DistanceX(g9,g7) = 5.5
    c: DistanceY(g13) = -13
FEATURE [PartDesign::Pocket] Pocket317
  BaseFeature = -> Pad099
  Direction = (0,1,-2e-16)
  Length = 5
  Length2 = 5
  Placement = pos=(0,0,0) rot=(1,0,0;1.5708rad)
  Profile = -> Sketch451
  ReferenceAxis = -> Sketch451 [N_Axis]
  Suppressed = false
  Type = 1
FEATURE [Sketcher::SketchObject] Sketch452
  ArcFitTolerance = 1e-06
  AttachmentSupport = -> [XZ_Plane289]
  FullyConstrained = true
  MakeInternals = false
  MapMode = 5
  Placement = pos=(0,0,0) rot=(1,0,0;1.5708rad)
  sketch-geometry (2):
    g0: Circle CenterX=-5 CenterY=-13 CenterZ=0 NormalX=0 NormalY=0 NormalZ=1 AngleXU=0 Radius=1.75
    g1: Circle CenterX=5 CenterY=-13 CenterZ=0 NormalX=0 NormalY=0 NormalZ=1 AngleXU=0 Radius=1.75
  constraints (5):
    c: Symmetric(g1,g0,g-2)
    c: Equal(g0,g1)
    c: Diameter(g1) = 3.5
    c: DistanceY(g1) = -13
    c: DistanceX(g0,g1) = 10
FEATURE [PartDesign::Pocket] Pocket318
  BaseFeature = -> Pocket317
  Direction = (0,1,-2e-16)
  Length = 5
  Length2 = 5
  Midplane = true
  Placement = pos=(0,0,0) rot=(1,0,0;1.5708rad)
  Profile = -> Sketch452
  ReferenceAxis = -> Sketch452 [N_Axis]
  Suppressed = false
  Type = 1
FEATURE [Sketcher::SketchObject] Sketch453
  ArcFitTolerance = 1e-06
  AttachmentSupport = -> [XY_Plane267]
  FullyConstrained = true
  MakeInternals = false
  MapMode = 5
  expr: Constraints[9] = -Spreadsheet.side_length / 2
  sketch-geometry (4):
    g0: LineSegment StartX=-10.2 StartY=-165.8 StartZ=0 EndX=-10.2 EndY=-170 EndZ=0
    g1: LineSegment StartX=-10.2 StartY=-170 StartZ=0 EndX=10.2 EndY=-170 EndZ=0
    g2: LineSegment StartX=10.2 StartY=-170 StartZ=0 EndX=10.2 EndY=-165.8 EndZ=0
    g3: LineSegment StartX=10.2 StartY=-165.8 StartZ=0 EndX=-10.2 EndY=-165.8 EndZ=0
  constraints (11):
    c: Coincident(g0,g1)
    c: Coincident(g1,g2)
    c: Coincident(g2,g3)
    c: Coincident(g3,g0)
    c: Vertical(g0)
    c: Vertical(g2)
    c: Horizontal(g1)
    c: Symmetric(g2,g0,g-2)
    c: DistanceX(g3,g3) = 20.4
    c: DistanceY(g1) = -170
    c: DistanceY(g2,g2) = 4.2
FEATURE [PartDesign::Pocket] Pocket319
  BaseFeature = -> Mirrored009
  Direction = (0,0,-1)
  Length = 5
  Length2 = 5
  Midplane = true
  Profile = -> Sketch453
  ReferenceAxis = -> Sketch453 [N_Axis]
  Suppressed = false
  Type = 1
FEATURE [Sketcher::SketchObject] Sketch454
  ArcFitTolerance = 1e-06
  AttachmentSupport = -> [YZ_Plane290]
  FullyConstrained = true
  MakeInternals = false
  MapMode = 5
  Placement = pos=(0,0,0) rot=(0.57735,0.57735,0.57735;2.0944rad)
  sketch-geometry (12):
    g0: LineSegment StartX=0 StartY=0 StartZ=0 EndX=5.72426 EndY=0 EndZ=0
    g1: LineSegment StartX=20 StartY=0 StartZ=0 EndX=20 EndY=-4 EndZ=0
    g2: LineSegment StartX=20 StartY=-4 StartZ=0 EndX=14 EndY=-10 EndZ=0
    g3: LineSegment StartX=14 StartY=-10 StartZ=0 EndX=0 EndY=-10 EndZ=0
    g4: LineSegment StartX=0 StartY=-10 StartZ=0 EndX=0 EndY=0 EndZ=0
    g5: LineSegment StartX=5.72426 StartY=0 StartZ=0 EndX=7.72426 EndY=2 EndZ=0
    g6: LineSegment StartX=7.72426 StartY=2 StartZ=0 EndX=12.2757 EndY=2 EndZ=0
    g7: LineSegment StartX=12.2757 StartY=2 StartZ=0 EndX=14.2757 EndY=0 EndZ=0
    g8: LineSegment StartX=14.2757 StartY=0 StartZ=0 EndX=20 EndY=0 EndZ=0
    g9: GeomPoint X=10 Y=2 Z=0
    g10: GeomPoint X=10 Y=0 Z=0
    g11: LineSegment [constr] StartX=7.3 StartY=2 StartZ=0 EndX=12.7 EndY=2 EndZ=0
  constraints (33):
    c: Coincident(g-1,g0)
    c: PointOnObject(g8,g-1)
    c: Coincident(g8,g1)
    c: Vertical(g1)
    c: Coincident(g1,g2)
    c: Coincident(g2,g3)
    c: PointOnObject(g3,g-2)
    c: Horizontal(g3)
    c: Coincident(g3,g4)
    c: Coincident(g4,g0)
    c: Angle(g2) = -2.35619
    c: DistanceX(g0,g8) = 20
    c: DistanceY(g1,g1) = 4
    c: DistanceY(g4,g4) = 10
    c: Coincident(g5,g6)
    c: Horizontal(g6)
    c: Coincident(g6,g7)
    c: PointOnObject(g7,g8)
    c: Coincident(g0,g5)
    c: PointOnObject(g8,g7)
    c: Horizontal(g8)
    c: Symmetric(g6,g6,g9)
    c: PointOnObject(g10,g-1)
    c: DistanceX(g10) = 10
    c: Vertical(g10,g9)
    c: Perpendicular(g5,g7)
    c: Angle(g5) = 0.785398
    c: DistanceY(g7,g7) = 2
    c: Horizontal(g11)
    c: Symmetric(g11,g11,g9)
    c: Distance(g11,g7) = 0.3
    c: DistanceX(g11,g11) = 5.4
    c: Horizontal(g0)
FEATURE [PartDesign::Pad] Pad100
  Direction = (1,0,0)
  Length = 20
  Length2 = 10
  Midplane = true
  Placement = pos=(0,0,0) rot=(1,1,1;2.0944rad)
  Profile = -> Sketch454
  ReferenceAxis = -> Sketch454 [N_Axis]
  Suppressed = false
  Type = 0
FEATURE [Sketcher::SketchObject] Sketch455
  ArcFitTolerance = 1e-06
  AttachmentSupport = -> [XZ_Plane290]
  FullyConstrained = true
  MakeInternals = false
  MapMode = 5
  Placement = pos=(0,0,0) rot=(1,0,0;1.5708rad)
  sketch-geometry (4):
    g0: LineSegment StartX=-6 StartY=2 StartZ=0 EndX=-6 EndY=0 EndZ=0
    g1: LineSegment StartX=-6 StartY=0 StartZ=0 EndX=6 EndY=0 EndZ=0
    g2: LineSegment StartX=6 StartY=0 StartZ=0 EndX=6 EndY=2 EndZ=0
    g3: LineSegment StartX=6 StartY=2 StartZ=0 EndX=-6 EndY=2 EndZ=0
  constraints (11):
    c: Coincident(g0,g1)
    c: Coincident(g1,g2)
    c: Coincident(g2,g3)
    c: Coincident(g3,g0)
    c: Vertical(g0)
    c: Vertical(g2)
    c: Horizontal(g3)
    c: Symmetric(g1,g0,g-2)
    c: PointOnObject(g1,g-1)
    c: DistanceY(g2,g2) = 2
    c: DistanceX(g3,g3) = 12
FEATURE [PartDesign::Pocket] Pocket320
  BaseFeature = -> Pad100
  Direction = (0,1,-2e-16)
  Length = 5
  Length2 = 5
  Midplane = true
  Placement = pos=(0,0,0) rot=(1,1,1;2.0944rad)
  Profile = -> Sketch455
  ReferenceAxis = -> Sketch455 [N_Axis]
  Refine = true
  Suppressed = false
  Type = 1
FEATURE [Sketcher::SketchObject] Sketch456
  ArcFitTolerance = 1e-06
  AttachmentOffset = pos=(0,0,-10) rot=(0,0,1;0rad)
  AttachmentSupport = -> [XZ_Plane290]
  FullyConstrained = true
  MakeInternals = false
  MapMode = 5
  Placement = pos=(0,10,-2.2e-15) rot=(1,0,0;1.5708rad)
  sketch-geometry (6):
    g0: LineSegment StartX=0 StartY=0 StartZ=0 EndX=2.75 EndY=0 EndZ=0
    g1: LineSegment StartX=2.75 StartY=0 StartZ=0 EndX=2.75 EndY=-4 EndZ=0
    g2: LineSegment StartX=2.75 StartY=-4 StartZ=0 EndX=5 EndY=-4 EndZ=0
    g3: LineSegment StartX=5 StartY=-4 StartZ=0 EndX=5 EndY=-10 EndZ=0
    g4: LineSegment StartX=5 StartY=-10 StartZ=0 EndX=0 EndY=-10 EndZ=0
    g5: LineSegment StartX=0 StartY=-10 StartZ=0 EndX=0 EndY=0 EndZ=0
  constraints (17):
    c: Coincident(g-1,g0)
    c: Horizontal(g0)
    c: Coincident(g0,g1)
    c: Vertical(g1)
    c: Coincident(g1,g2)
    c: Horizontal(g2)
    c: Coincident(g2,g3)
    c: Vertical(g3)
    c: Coincident(g3,g4)
    c: PointOnObject(g4,g-2)
    c: Horizontal(g4)
    c: Coincident(g4,g5)
    c: Coincident(g5,g0)
    c: DistanceY(g5,g5) = 10
    c: DistanceX(g4,g4) = 5
    c: DistanceX(g0,g0) = 2.75
    c: DistanceY(g1,g1) = 4
FEATURE [PartDesign::Groove] Groove017
  Angle = 360
  Angle2 = 60
  Axis = (0,2e-16,1)
  Base = (0,10,-2.2e-15)
  BaseFeature = -> Pocket320
  Placement = pos=(0,0,0) rot=(1,1,1;2.0944rad)
  Profile = -> Sketch456
  ReferenceAxis = -> Sketch456 [V_Axis]
  Suppressed = false
  Type = 0
FEATURE [Sketcher::SketchObject] Sketch466
  ArcFitTolerance = 1e-06
  AttachmentSupport = -> [XZ_Plane280]
  FullyConstrained = true
  MakeInternals = false
  MapMode = 5
  Placement = pos=(0,0,0) rot=(1,0,0;1.5708rad)
  sketch-geometry (10):
    g0: GeomPoint X=-50 Y=0 Z=0
    g1: Circle CenterX=-26 CenterY=-25 CenterZ=0 NormalX=0 NormalY=0 NormalZ=1 AngleXU=0 Radius=1.75
    g2: Circle CenterX=-80 CenterY=15 CenterZ=0 NormalX=0 NormalY=0 NormalZ=1 AngleXU=0 Radius=1.75
    g3: Circle CenterX=60 CenterY=0 CenterZ=0 NormalX=0 NormalY=0 NormalZ=1 AngleXU=0 Radius=57
    g4: Circle CenterX=12 CenterY=48 CenterZ=0 NormalX=0 NormalY=0 NormalZ=1 AngleXU=0 Radius=2
    g5: Circle CenterX=108 CenterY=48 CenterZ=0 NormalX=0 NormalY=0 NormalZ=1 AngleXU=0 Radius=2
    g6: Circle CenterX=108 CenterY=-48 CenterZ=0 NormalX=0 NormalY=0 NormalZ=1 AngleXU=0 Radius=2
    g7: Circle CenterX=12 CenterY=-48 CenterZ=0 NormalX=0 NormalY=0 NormalZ=1 AngleXU=0 Radius=2
    g8: LineSegment [constr] StartX=12 StartY=48 StartZ=0 EndX=12 EndY=-48 EndZ=0
    g9: LineSegment [constr] StartX=12 StartY=48 StartZ=0 EndX=108 EndY=48 EndZ=0
  constraints (25):
    c: PointOnObject(g0,g-1)
    c: DistanceX(g0) = -50
    c: Equal(g1,g2)
    c: DistanceX(g0,g1) = 24
    c: Diameter(g2) = 3.5
    c: DistanceY(g1) = -25
    c: DistanceY(g2) = 15
    c: DistanceX(g2) = -80
    c: Symmetric(g7,g5,g3)
    c: Symmetric(g4,g6,g3)
    c: Horizontal(g4,g5)
    c: Vertical(g7,g4)
    c: Coincident(g8,g4)
    c: Coincident(g8,g7)
    c: Coincident(g9,g4)
    c: Coincident(g9,g5)
    c: Equal(g9,g8)
    c: Equal(g4,g5)
    c: Equal(g4,g6)
    c: Equal(g4,g7)
    c: Diameter(g4) = 4
    c: Diameter(g3) = 114
    c: DistanceX(g9,g9) = 96
    c: PointOnObject(g3,g-1)
    c: DistanceX(g3) = 60
FEATURE [PartDesign::Pocket] Pocket330
  BaseFeature = -> Mirrored010
  Direction = (0,1,-2e-16)
  Length = 5
  Length2 = 5
  Midplane = true
  Placement = pos=(0,0,0) rot=(1,0,0;1.5708rad)
  Profile = -> Sketch466
  ReferenceAxis = -> Sketch466 [N_Axis]
  Suppressed = false
  Type = 1
FEATURE [PartDesign::Body] Body143  label="panel-back"
  AllowCompound = false
  Group = -> [Sketch426,Pad091,Sketch427,Pocket299,Mirrored010,Sketch466,Pocket330]
  Origin = -> Origin281
  Placement = pos=(0,170,0) rot=(0,0,1;0rad)
  Tip = -> Pocket330
  expr: .Placement.Base.y = Spreadsheet.side_length / 2
FEATURE [Sketcher::SketchObject] Sketch473
  ArcFitTolerance = 1e-06
  AttachmentSupport = -> [XY_Plane267]
  FullyConstrained = true
  MakeInternals = false
  MapMode = 5
  expr: Constraints[12] = -Spreadsheet.side_length / 2
  sketch-geometry (6):
    g0: LineSegment StartX=-150 StartY=-60 StartZ=0 EndX=-150 EndY=-80 EndZ=0
    g1: LineSegment StartX=-150 StartY=-80 StartZ=0 EndX=-145 EndY=-80 EndZ=0
    g2: LineSegment StartX=-145 StartY=-80 StartZ=0 EndX=-145 EndY=-60 EndZ=0
    g3: LineSegment StartX=-145 StartY=-60 StartZ=0 EndX=-150 EndY=-60 EndZ=0
    g4: GeomPoint X=-150 Y=-70 Z=0
    g5: GeomPoint X=-170 Y=0 Z=0
  constraints (15):
    c: Coincident(g0,g1)
    c: Coincident(g1,g2)
    c: Coincident(g2,g3)
    c: Coincident(g3,g0)
    c: Vertical(g0)
    c: Vertical(g2)
    c: Horizontal(g1)
    c: Horizontal(g3)
    c: Symmetric(g0,g0,g4)
    c: DistanceY(g4) = -70
    c: DistanceY(g2,g2) = 20
    c: PointOnObject(g5,g-1)
    c: DistanceX(g5) = -170
    c: DistanceX(g5,g0) = 20
    c: DistanceX(g3,g3) = 5
FEATURE [PartDesign::Pocket] Pocket335
  BaseFeature = -> Pocket319
  Direction = (0,0,-1)
  Length = 5
  Length2 = 5
  Midplane = true
  Profile = -> Sketch473
  ReferenceAxis = -> Sketch473 [N_Axis]
  Suppressed = false
  Type = 1
FEATURE [PartDesign::Body] Body132  label="panel-bottom-lid"
  AllowCompound = false
  Group = -> [Sketch405,Pad088,Sketch406,Pocket281,PolarPattern004,Sketch407,Pocket282,Mirrored009,Sketch453,Pocket319,Sketch473,Pocket335]
  Origin = -> Origin268
  Placement = pos=(0,0,-170) rot=(0,0,1;0rad)
  Tip = -> Pocket335
  expr: .Placement.Base.z = -Spreadsheet.height / 2 + 50
FEATURE [Sketcher::SketchObject] Sketch483
  ArcFitTolerance = 1e-06
  AttachmentSupport = -> [XZ_Plane289]
  FullyConstrained = true
  MakeInternals = false
  MapMode = 5
  Placement = pos=(0,0,0) rot=(1,0,0;1.5708rad)
  sketch-geometry (2):
    g0: Circle CenterX=5 CenterY=5 CenterZ=0 NormalX=0 NormalY=0 NormalZ=1 AngleXU=0 Radius=3
    g1: Circle CenterX=-5 CenterY=5 CenterZ=0 NormalX=0 NormalY=0 NormalZ=1 AngleXU=0 Radius=3
  constraints (5):
    c: Equal(g0,g1)
    c: Symmetric(g1,g0,g-2)
    c: DistanceX(g1,g0) = 10
    c: DistanceY(g0) = 5
    c: Diameter(g0) = 6
FEATURE [PartDesign::Pocket] Pocket339
  BaseFeature = -> Pocket318
  Direction = (0,1,-2e-16)
  Length = 4
  Length2 = 5
  Placement = pos=(0,0,0) rot=(1,0,0;1.5708rad)
  Profile = -> Sketch483
  ReferenceAxis = -> Sketch483 [N_Axis]
  Suppressed = false
  Type = 0
FEATURE [PartDesign::Body] Body151  label="lower-door-stopper"
  AllowCompound = false
  Group = -> [Sketch450,Pad099,Sketch451,Pocket317,Sketch452,Pocket318,Sketch483,Pocket339]
  Origin = -> Origin290
  Placement = pos=(0,-170,-165) rot=(0,0,1;0rad)
  Tip = -> Pocket339
  expr: .Placement.Base.y = -Spreadsheet.side_length / 2
  expr: .Placement.Base.z = -Spreadsheet.height / 2 + 55
FEATURE [Sketcher::SketchObject] Sketch484
  ArcFitTolerance = 1e-06
  AttachmentSupport = -> [XZ_Plane290]
  FullyConstrained = true
  MakeInternals = false
  MapMode = 5
  Placement = pos=(0,0,0) rot=(1,0,0;1.5708rad)
  sketch-geometry (2):
    g0: Circle CenterX=-5 CenterY=-5 CenterZ=0 NormalX=0 NormalY=0 NormalZ=1 AngleXU=0 Radius=3
    g1: Circle CenterX=5 CenterY=-5 CenterZ=0 NormalX=0 NormalY=0 NormalZ=1 AngleXU=0 Radius=3
  constraints (5):
    c: Symmetric(g1,g0,g-2)
    c: Equal(g1,g0)
    c: DistanceX(g1) = 5
    c: DistanceY(g1) = -5
    c: Diameter(g1) = 6
FEATURE [PartDesign::Pocket] Pocket340
  BaseFeature = -> Groove017
  Direction = (0,1,-2e-16)
  Length = 4
  Length2 = 5
  Placement = pos=(0,0,0) rot=(1,1,1;2.0944rad)
  Profile = -> Sketch484
  ReferenceAxis = -> Sketch484 [N_Axis]
  Suppressed = false
  Type = 0
FEATURE [PartDesign::Body] Body152  label="upper-door-stopper"
  AllowCompound = false
  Group = -> [Sketch454,Pad100,Sketch455,Pocket320,Sketch456,Groove017,Sketch484,Pocket340]
  Origin = -> Origin291
  Placement = pos=(0,-170,200) rot=(0,0,1;0rad)
  Tip = -> Pocket340
  expr: .Placement.Base.y = -Spreadsheet.side_length / 2
  expr: .Placement.Base.z = Spreadsheet.height / 2 - 20
COMPONENT P25 — geometry summary ("endstop-z"; no construction recipe available for this part):
  bounding box: 22.0 x 20.0 x 8.0 mm
  tessellated surface: 568 triangles
  volume: 1386 mm^3 (39% of its bounding box)
PROVENANCE & LICENSES
A FreeCAD (.FCStd) document from a public repository crawl; recipes are the document's own serialized feature recipes (and, for linked parts, companion documents' recipes).
License: as declared in the source repository (recorded in the dataset sidecar).
